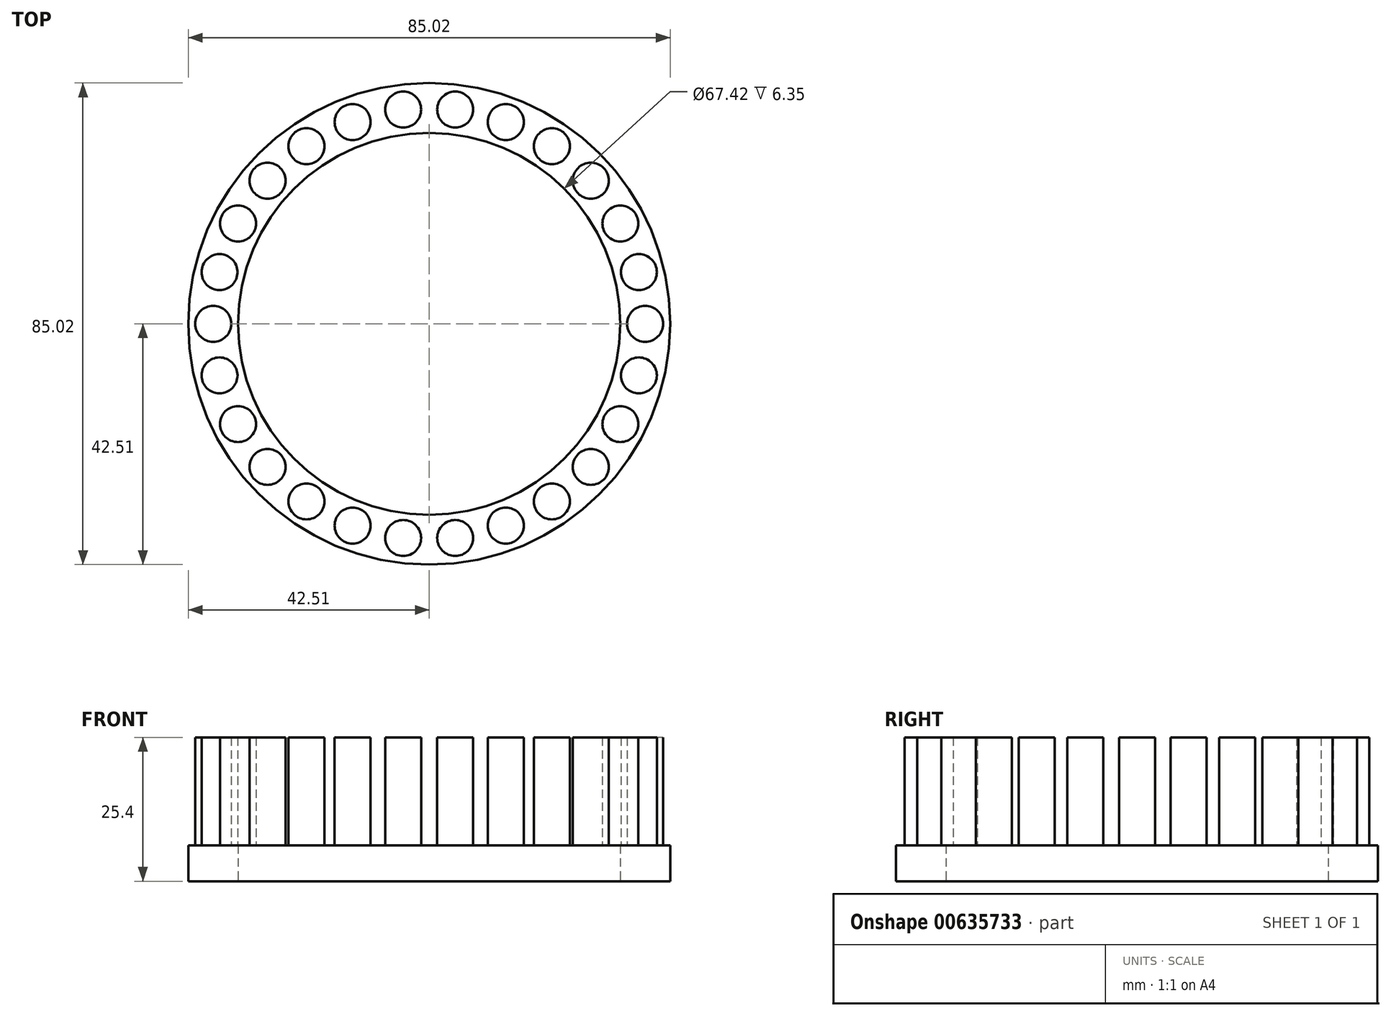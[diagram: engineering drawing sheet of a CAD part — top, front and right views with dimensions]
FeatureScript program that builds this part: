
annotation { "Feature Type Name" : "Feature", "Feature Type Description" : "" }
export const myFeature = defineFeature(function(context is Context, id is Id, definition is map)
    precondition{}
    {
        {
            var Q0;
            Q0=qCreatedBy(makeId("Top.planeOp"),FACE);
            var sketch = newSketch(context, id + "F0", { "sketchPlane" : qUnion([Q0])});
            skCircle(sketch, "E0", {"center": v(0, 0) * mm, "radius": 38.1 * mm, "construction": true});
            skCircle(sketch, "E1", {"center": v(38.1, 0) * mm, "radius": 3.18 * mm});
            skCircle(sketch, "E2", {"center": v(37, -9.12) * mm, "radius": 3.18 * mm});
            skCircle(sketch, "E3", {"center": v(33.74, -17.7) * mm, "radius": 3.18 * mm});
            skCircle(sketch, "E4", {"center": v(28.52, -25.26) * mm, "radius": 3.18 * mm});
            skCircle(sketch, "E5", {"center": v(21.64, -31.36) * mm, "radius": 3.18 * mm});
            skCircle(sketch, "E6", {"center": v(13.51, -35.62) * mm, "radius": 3.18 * mm});
            skCircle(sketch, "E7", {"center": v(4.6, -37.82) * mm, "radius": 3.18 * mm});
            skCircle(sketch, "E8", {"center": v(-4.6, -37.82) * mm, "radius": 3.18 * mm});
            skCircle(sketch, "E9", {"center": v(-13.51, -35.62) * mm, "radius": 3.18 * mm});
            skCircle(sketch, "E10", {"center": v(-21.64, -31.36) * mm, "radius": 3.18 * mm});
            skCircle(sketch, "E11", {"center": v(-28.52, -25.26) * mm, "radius": 3.18 * mm});
            skCircle(sketch, "E12", {"center": v(-33.74, -17.7) * mm, "radius": 3.18 * mm});
            skCircle(sketch, "E13", {"center": v(-37, -9.12) * mm, "radius": 3.18 * mm});
            skCircle(sketch, "E14", {"center": v(-38.1, 0) * mm, "radius": 3.18 * mm});
            skCircle(sketch, "E15", {"center": v(-37, 9.12) * mm, "radius": 3.18 * mm});
            skCircle(sketch, "E16", {"center": v(-33.74, 17.7) * mm, "radius": 3.18 * mm});
            skCircle(sketch, "E17", {"center": v(-28.52, 25.26) * mm, "radius": 3.18 * mm});
            skCircle(sketch, "E18", {"center": v(-21.64, 31.36) * mm, "radius": 3.18 * mm});
            skCircle(sketch, "E19", {"center": v(-13.51, 35.62) * mm, "radius": 3.18 * mm});
            skCircle(sketch, "E20", {"center": v(-4.6, 37.82) * mm, "radius": 3.18 * mm});
            skCircle(sketch, "E21", {"center": v(4.6, 37.82) * mm, "radius": 3.18 * mm});
            skCircle(sketch, "E22", {"center": v(13.51, 35.62) * mm, "radius": 3.18 * mm});
            skCircle(sketch, "E23", {"center": v(21.64, 31.36) * mm, "radius": 3.18 * mm});
            skCircle(sketch, "E24", {"center": v(28.52, 25.26) * mm, "radius": 3.18 * mm});
            skCircle(sketch, "E25", {"center": v(33.74, 17.7) * mm, "radius": 3.18 * mm});
            skCircle(sketch, "E26", {"center": v(37, 9.12) * mm, "radius": 3.18 * mm});
            skLineSegment(sketch, "E27", {"start": v(-13.51, 35.62) * mm, "end": v(-4.6, 37.82) * mm, "construction": true});
            skLineSegment(sketch, "E28", {"start": v(4.6, 37.82) * mm, "end": v(-4.6, 37.82) * mm, "construction": true});
            skLineSegment(sketch, "E29", {"start": v(13.51, 35.62) * mm, "end": v(21.64, 31.36) * mm, "construction": true});
            skLineSegment(sketch, "E30", {"start": v(21.64, 31.36) * mm, "end": v(28.52, 25.26) * mm, "construction": true});
            skLineSegment(sketch, "E31", {"start": v(28.52, 25.26) * mm, "end": v(33.74, 17.7) * mm, "construction": true});
            skLineSegment(sketch, "E32", {"start": v(33.74, 17.7) * mm, "end": v(37, 9.12) * mm, "construction": true});
            skLineSegment(sketch, "E33", {"start": v(37, 9.12) * mm, "end": v(38.1, 0) * mm, "construction": true});
            skLineSegment(sketch, "E34", {"start": v(38.1, 0) * mm, "end": v(37, -9.12) * mm, "construction": true});
            skLineSegment(sketch, "E35", {"start": v(37, -9.12) * mm, "end": v(33.74, -17.7) * mm, "construction": true});
            skLineSegment(sketch, "E36", {"start": v(33.74, -17.7) * mm, "end": v(28.52, -25.26) * mm, "construction": true});
            skLineSegment(sketch, "E37", {"start": v(28.52, -25.26) * mm, "end": v(21.64, -31.36) * mm, "construction": true});
            skLineSegment(sketch, "E38", {"start": v(21.64, -31.36) * mm, "end": v(13.51, -35.62) * mm, "construction": true});
            skLineSegment(sketch, "E39", {"start": v(13.51, -35.62) * mm, "end": v(4.6, -37.82) * mm, "construction": true});
            skLineSegment(sketch, "E40", {"start": v(4.6, -37.82) * mm, "end": v(-4.6, -37.82) * mm, "construction": true});
            skLineSegment(sketch, "E41", {"start": v(-4.6, -37.82) * mm, "end": v(-13.51, -35.62) * mm, "construction": true});
            skLineSegment(sketch, "E42", {"start": v(-13.51, -35.62) * mm, "end": v(-21.64, -31.36) * mm, "construction": true});
            skLineSegment(sketch, "E43", {"start": v(-21.64, -31.36) * mm, "end": v(-28.52, -25.26) * mm, "construction": true});
            skLineSegment(sketch, "E44", {"start": v(-28.52, -25.26) * mm, "end": v(-33.74, -17.7) * mm, "construction": true});
            skLineSegment(sketch, "E45", {"start": v(-33.74, -17.7) * mm, "end": v(-37, -9.12) * mm, "construction": true});
            skLineSegment(sketch, "E46", {"start": v(-37, -9.12) * mm, "end": v(-38.1, 0) * mm, "construction": true});
            skLineSegment(sketch, "E47", {"start": v(-38.1, 0) * mm, "end": v(-37, 9.12) * mm, "construction": true});
            skLineSegment(sketch, "E48", {"start": v(-37, 9.12) * mm, "end": v(-33.74, 17.7) * mm, "construction": true});
            skLineSegment(sketch, "E49", {"start": v(-33.74, 17.7) * mm, "end": v(-28.52, 25.26) * mm, "construction": true});
            skLineSegment(sketch, "E50", {"start": v(-21.64, 31.36) * mm, "end": v(-28.52, 25.26) * mm, "construction": true});
            skLineSegment(sketch, "E51", {"start": v(-13.51, 35.62) * mm, "end": v(-21.64, 31.36) * mm, "construction": true});
            skLineSegment(sketch, "E52", {"start": v(4.6, 37.82) * mm, "end": v(13.51, 35.62) * mm, "construction": true});
            skSolve(sketch);
        }
        {
            var Q0;
            Q0=qCreatedBy(makeId("Top.planeOp"),FACE);
            var sketch = newSketch(context, id + "F1", { "sketchPlane" : qUnion([Q0])});
            skCircle(sketch, "E53", {"center": v(0, 0) * mm, "radius": 38.1 * mm, "construction": true});
            skCircle(sketch, "E54", {"center": v(0, 0) * mm, "radius": 42.5 * mm});
            skCircle(sketch, "E55", {"center": v(0, 0) * mm, "radius": 33.7 * mm});
            skLineSegment(sketch, "E56", {"start": v(-38.1, 0) * mm, "end": v(-42.5, 0) * mm, "construction": true});
            skLineSegment(sketch, "E57", {"start": v(-33.7, 0) * mm, "end": v(-38.1, 0) * mm, "construction": true});
            skSolve(sketch);
        }
        {
            var Q0;
            Q0 = qSketchRegion(id + "F1", true);
            extrude(context, id + "F2", {"entities" : qUnion([Q0]), "depth" : 6.35 * mm, "offsetDistance" : 25.4 * mm});
        }
        {
            var Q0;
            Q0 = qSketchRegion(id + "F0", true);
            extrude(context, id + "F3", {"entities" : qUnion([Q0]), "operationType" : NewBodyOperationType.ADD, "depth" : 25.4 * mm, "offsetDistance" : 25.4 * mm});
        }
    });
